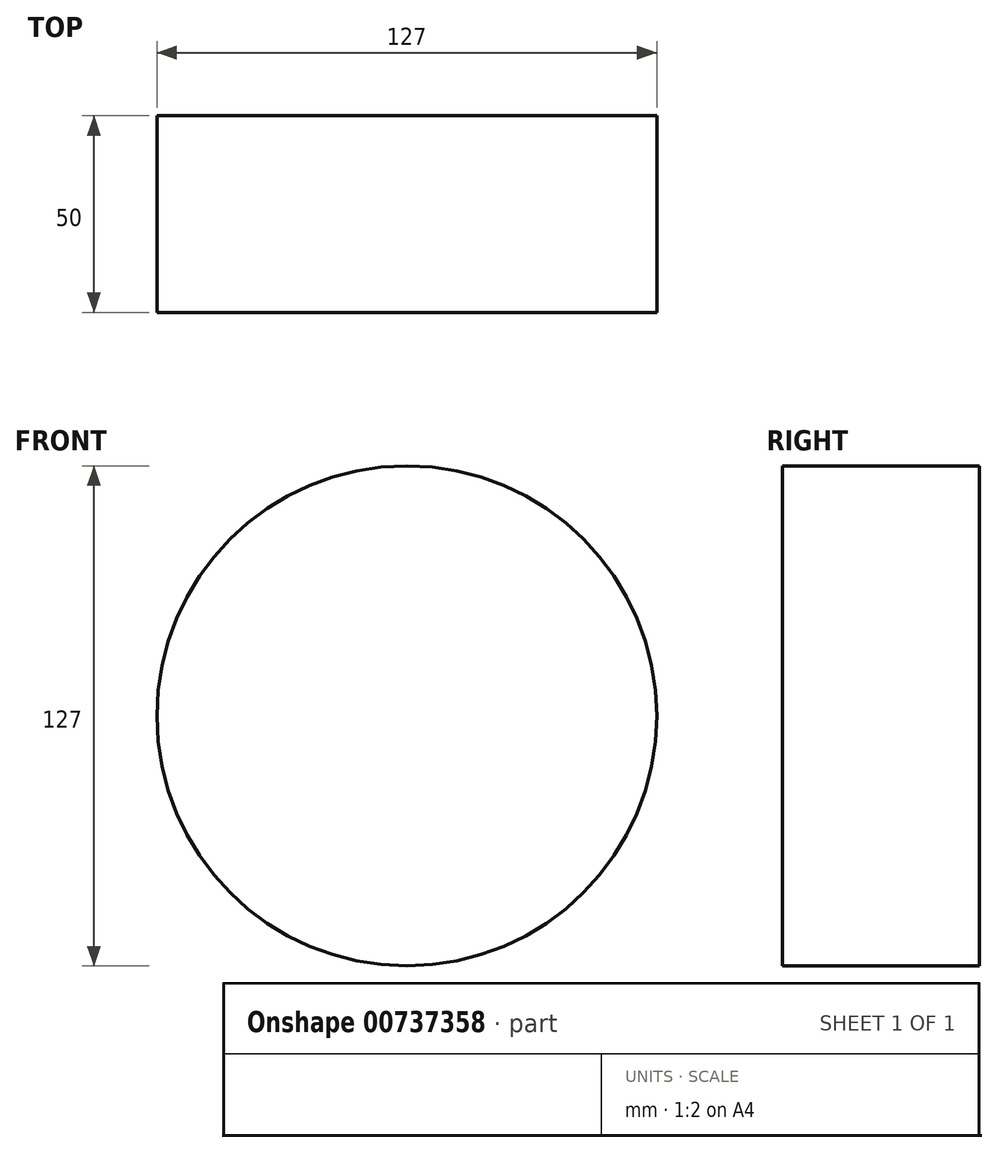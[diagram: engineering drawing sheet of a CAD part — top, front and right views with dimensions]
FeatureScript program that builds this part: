
annotation { "Feature Type Name" : "Feature", "Feature Type Description" : "" }
export const myFeature = defineFeature(function(context is Context, id is Id, definition is map)
    precondition{}
    {
        {
            var Q0;
            Q0=qCreatedBy(makeId("Front.planeOp"),FACE);
            var sketch = newSketch(context, id + "F0", { "sketchPlane" : qUnion([Q0])});
            skCircle(sketch, "E0", {"center": v(0, 0) * mm, "radius": 63.5 * mm});
            skSolve(sketch);
        }
        {
            var Q0;
            Q0=makeQuery(id+"F0.imprint","IMPRINT",FACE,{"disambiguationData":[TD([[makeQuery(id+"F0.imprint","IMPRINT",EDGE,{"derivedFrom":sQuery(id+"F0.wireOp",EDGE,"E0")}),1.0]])]});
            extrude(context, id + "F1", {"entities" : qUnion([Q0]), "depth" : 50 * mm, "offsetDistance" : 25.4 * mm});
        }
    });
